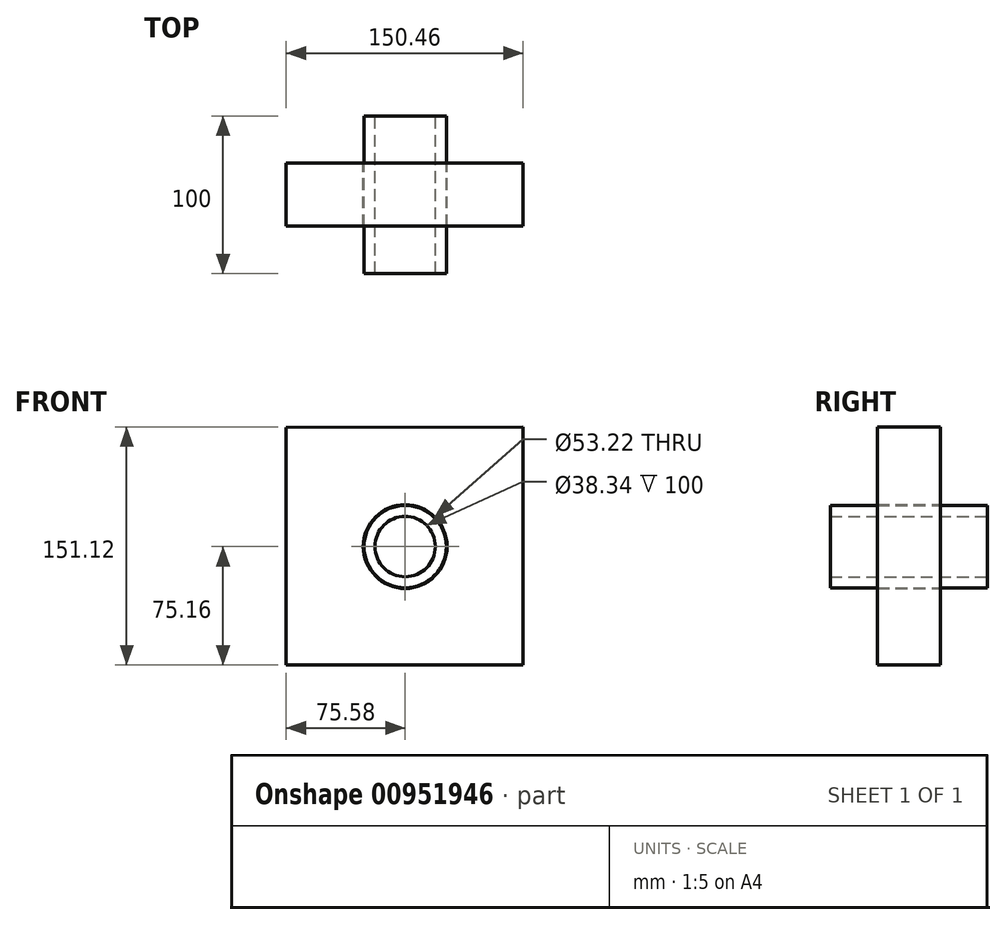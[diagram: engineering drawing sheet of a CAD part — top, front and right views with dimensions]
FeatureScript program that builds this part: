
annotation { "Feature Type Name" : "Feature", "Feature Type Description" : "" }
export const myFeature = defineFeature(function(context is Context, id is Id, definition is map)
    precondition{}
    {
        {
            var Q0;
            Q0=qCreatedBy(makeId("Front.planeOp"),FACE);
            var sketch = newSketch(context, id + "F0", { "sketchPlane" : qUnion([Q0])});
            skCircle(sketch, "E0", {"center": v(0, 0) * mm, "radius": 19.17 * mm});
            skCircle(sketch, "E1", {"center": v(0, 0) * mm, "radius": 26.14 * mm});
            skSolve(sketch);
        }
        {
            var Q0;
            Q0 = qSketchRegion(id + "F0", true);
            extrude(context, id + "F1", {"entities" : qUnion([Q0]), "endBound" : BoundingType.SYMMETRIC, "depth" : 100 * mm, "offsetDistance" : 25 * mm});
        }
        {
            var Q0;
            Q0=qCreatedBy(makeId("Front.planeOp"),FACE);
            var sketch = newSketch(context, id + "F2", { "sketchPlane" : qUnion([Q0])});
            skLineSegment(sketch, "E2", {"start": v(-75.26, 75.37) * mm, "end": v(74.83, 75.37) * mm});
            skLineSegment(sketch, "E3", {"start": v(74.83, 75.37) * mm, "end": v(74.83, -74.72) * mm});
            skLineSegment(sketch, "E4", {"start": v(74.83, -74.72) * mm, "end": v(-75.26, -74.72) * mm});
            skLineSegment(sketch, "E5", {"start": v(-75.26, -74.72) * mm, "end": v(-75.26, 75.37) * mm});
            skSolve(sketch);
        }
        {
            var Q0;
            Q0=makeQuery(id+"F2.imprint","IMPRINT",FACE,{"disambiguationData":[TD([[makeQuery(id+"F2.imprint","IMPRINT",EDGE,{"derivedFrom":sQuery(id+"F2.wireOp",EDGE,"E2")}),-1.0]])]});
            var sketch = newSketch(context, id + "F3", { "sketchPlane" : qUnion([Q0])});
            skCircle(sketch, "E6", {"center": v(0, 0) * mm, "radius": 26.61 * mm});
            skLineSegment(sketch, "E7", {"start": v(-75.58, 75.75) * mm, "end": v(-75.58, -75.16) * mm});
            skLineSegment(sketch, "E8", {"start": v(-75.58, -75.16) * mm, "end": v(74.88, -75.16) * mm});
            skLineSegment(sketch, "E9", {"start": v(74.88, -75.16) * mm, "end": v(74.88, 75.96) * mm});
            skLineSegment(sketch, "E10", {"start": v(74.88, 75.96) * mm, "end": v(-75.58, 75.75) * mm});
            skSolve(sketch);
        }
        {
            var Q0;
            Q0 = qSketchRegion(id + "F3", true);
            extrude(context, id + "F4", {"entities" : qUnion([Q0]), "endBound" : BoundingType.SYMMETRIC, "depth" : 40 * mm, "offsetDistance" : 25 * mm});
        }
    });
